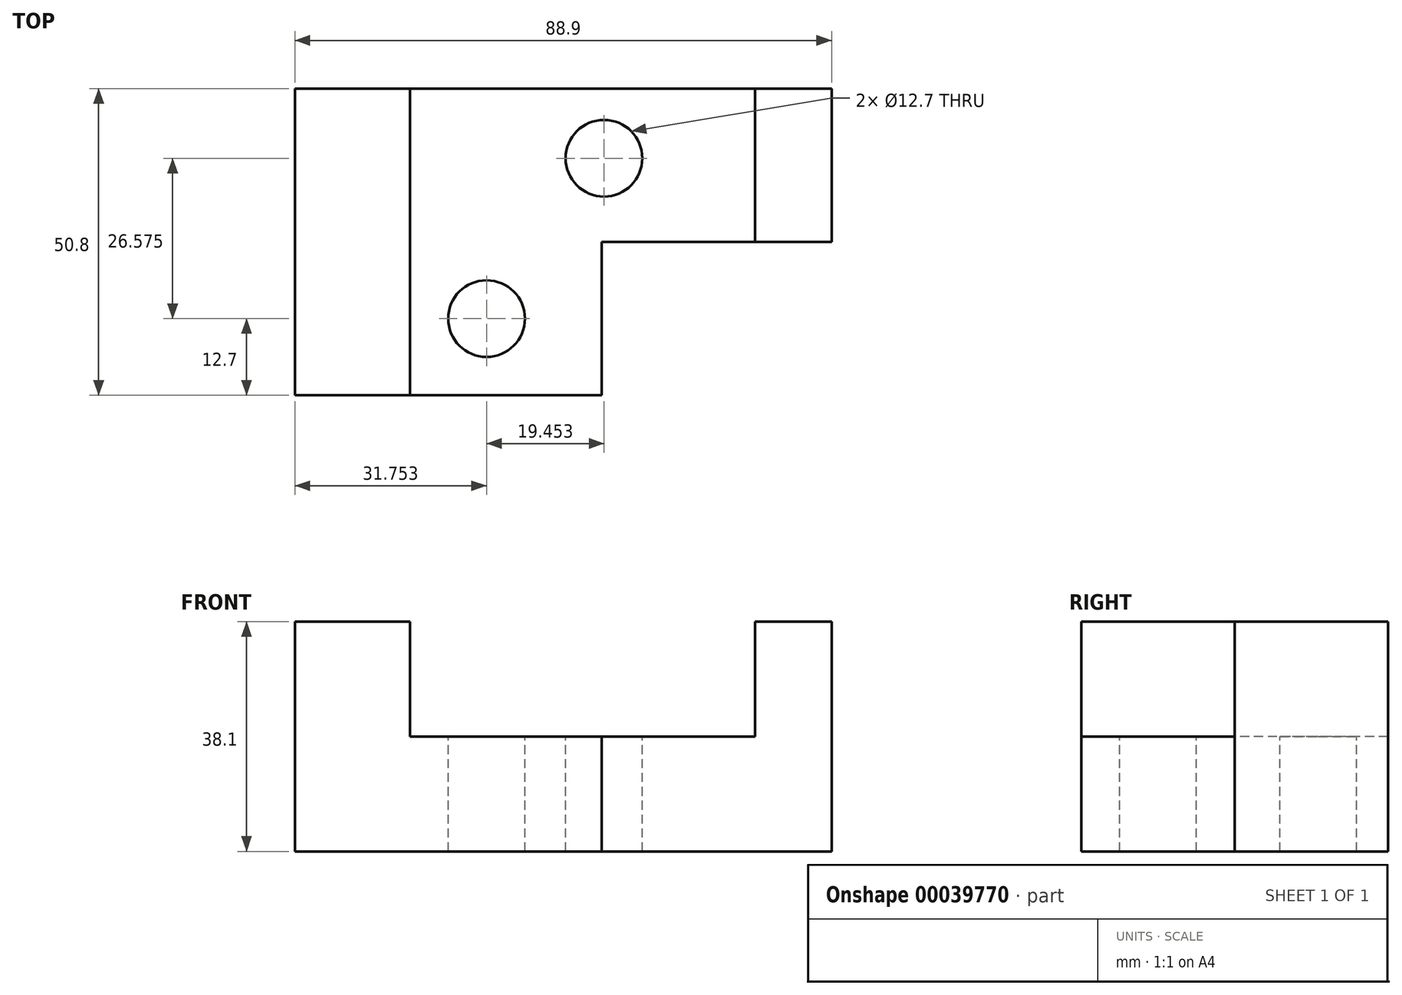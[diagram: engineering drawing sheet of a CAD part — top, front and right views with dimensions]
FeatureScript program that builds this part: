
annotation { "Feature Type Name" : "Feature", "Feature Type Description" : "" }
export const myFeature = defineFeature(function(context is Context, id is Id, definition is map)
    precondition{}
    {
        {
            var Q0;
            Q0=qCreatedBy(makeId("Front.planeOp"),FACE);
            var sketch = newSketch(context, id + "F0", { "sketchPlane" : qUnion([Q0])});
            skLineSegment(sketch, "E0", {"start": v(-99.27, 9.03) * mm, "end": v(-99.27, -29.07) * mm});
            skLineSegment(sketch, "E1", {"start": v(-99.27, -29.07) * mm, "end": v(-10.37, -29.07) * mm});
            skLineSegment(sketch, "E2", {"start": v(-10.37, -29.07) * mm, "end": v(-10.37, 9.03) * mm});
            skLineSegment(sketch, "E3", {"start": v(-10.37, 9.03) * mm, "end": v(-23.07, 9.03) * mm});
            skLineSegment(sketch, "E4", {"start": v(-23.07, 9.03) * mm, "end": v(-23.07, -10.02) * mm});
            skLineSegment(sketch, "E5", {"start": v(-23.07, -10.02) * mm, "end": v(-80.22, -10.02) * mm});
            skLineSegment(sketch, "E6", {"start": v(-80.22, -10.02) * mm, "end": v(-80.22, 9.03) * mm});
            skLineSegment(sketch, "E7", {"start": v(-80.22, 9.03) * mm, "end": v(-99.27, 9.03) * mm});
            skSolve(sketch);
        }
        {
            var Q0;
            Q0=makeQuery(id+"F0.imprint","IMPRINT",FACE,{"disambiguationData":[TD([[makeQuery(id+"F0.imprint","IMPRINT",EDGE,{"derivedFrom":sQuery(id+"F0.wireOp",EDGE,"E0")}),1.0]])]});
            extrude(context, id + "F1", {"entities" : qUnion([Q0]), "oppositeDirection" : true, "depth" : 50.8 * mm});
        }
        {
            var Q0;
            Q0=makeQuery(id+"F1.opExtrude","SWEPT_FACE",FACE,{"disambiguationData":[OSD([sQuery(id+"F0.wireOp",EDGE,"E1")])]});
            var sketch = newSketch(context, id + "F2", { "sketchPlane" : qUnion([Q0])});
            skLineSegment(sketch, "E8", {"start": v(-48.47, 0) * mm, "end": v(-48.47, -25.4) * mm});
            skLineSegment(sketch, "E9", {"start": v(-48.47, -25.4) * mm, "end": v(-10.37, -25.4) * mm});
            skLineSegment(sketch, "E10", {"start": v(-10.37, -25.4) * mm, "end": v(-10.37, 0) * mm});
            skLineSegment(sketch, "E11", {"start": v(-10.37, 0) * mm, "end": v(-48.47, 0) * mm});
            skSolve(sketch);
        }
        {
            var Q0;
            Q0=makeQuery(id+"F2.imprint","IMPRINT",FACE,{"disambiguationData":[TD([[makeQuery(id+"F2.imprint","IMPRINT",EDGE,{"derivedFrom":sQuery(id+"F2.wireOp",EDGE,"E8")}),1.0]])]});
            extrude(context, id + "F3", {"entities" : qUnion([Q0]), "operationType" : NewBodyOperationType.REMOVE, "oppositeDirection" : true, "depth" : 39.2 * mm});
        }
        {
            var Q0;
            Q0=makeQuery(id+"F1.opExtrude","SWEPT_FACE",FACE,{"disambiguationData":[OSD([sQuery(id+"F0.wireOp",EDGE,"E5")])]});
            var sketch = newSketch(context, id + "F4", { "sketchPlane" : qUnion([Q0])});
            skCircle(sketch, "E12", {"center": v(-67.52, 12.7) * mm, "radius": 1.42 * mm});
            skSolve(sketch);
        }
        {
            var Q0;
            Q0=sQuery(id+"F4.wireOp",VERTEX,"E12.center");
            var Q1;
            Q1=makeQuery(id+"F1.opExtrude","SWEPT_BODY",BODY,{"disambiguationData":[OSD([sQuery(id+"F0.wireOp",EDGE,"E0"),sQuery(id+"F0.wireOp",EDGE,"E1"),sQuery(id+"F0.wireOp",EDGE,"E2"),sQuery(id+"F0.wireOp",EDGE,"E3"),sQuery(id+"F0.wireOp",EDGE,"E4"),sQuery(id+"F0.wireOp",EDGE,"E5"),sQuery(id+"F0.wireOp",EDGE,"E6"),sQuery(id+"F0.wireOp",EDGE,"E7")])]});
            hole(context, id + "F5", {"style" : HoleStyle.SIMPLE, "holeDiameter" : 12.7 * mm, "endStyle" : HoleEndStyle.THROUGH, "locations" : qUnion([Q0]), "scope" : qUnion([Q1])});
        }
        {
            var Q0;
            Q0=makeQuery(id+"F1.opExtrude","SWEPT_FACE",FACE,{"disambiguationData":[OSD([sQuery(id+"F0.wireOp",EDGE,"E5")])]});
            var sketch = newSketch(context, id + "F6", { "sketchPlane" : qUnion([Q0])});
            skPoint(sketch, "E13", {"position": v(-48.06, 39.28) * mm});
            skSolve(sketch);
        }
        {
            var Q0;
            Q0=sQuery(id+"F6.wireOp",VERTEX,"E13");
            var Q1;
            Q1=makeQuery(id+"F1.opExtrude","SWEPT_BODY",BODY,{"disambiguationData":[OSD([sQuery(id+"F0.wireOp",EDGE,"E0"),sQuery(id+"F0.wireOp",EDGE,"E1"),sQuery(id+"F0.wireOp",EDGE,"E2"),sQuery(id+"F0.wireOp",EDGE,"E3"),sQuery(id+"F0.wireOp",EDGE,"E4"),sQuery(id+"F0.wireOp",EDGE,"E5"),sQuery(id+"F0.wireOp",EDGE,"E6"),sQuery(id+"F0.wireOp",EDGE,"E7")])]});
            hole(context, id + "F7", {"style" : HoleStyle.SIMPLE, "holeDiameter" : 12.7 * mm, "endStyle" : HoleEndStyle.THROUGH, "locations" : qUnion([Q0]), "scope" : qUnion([Q1])});
        }
    });
